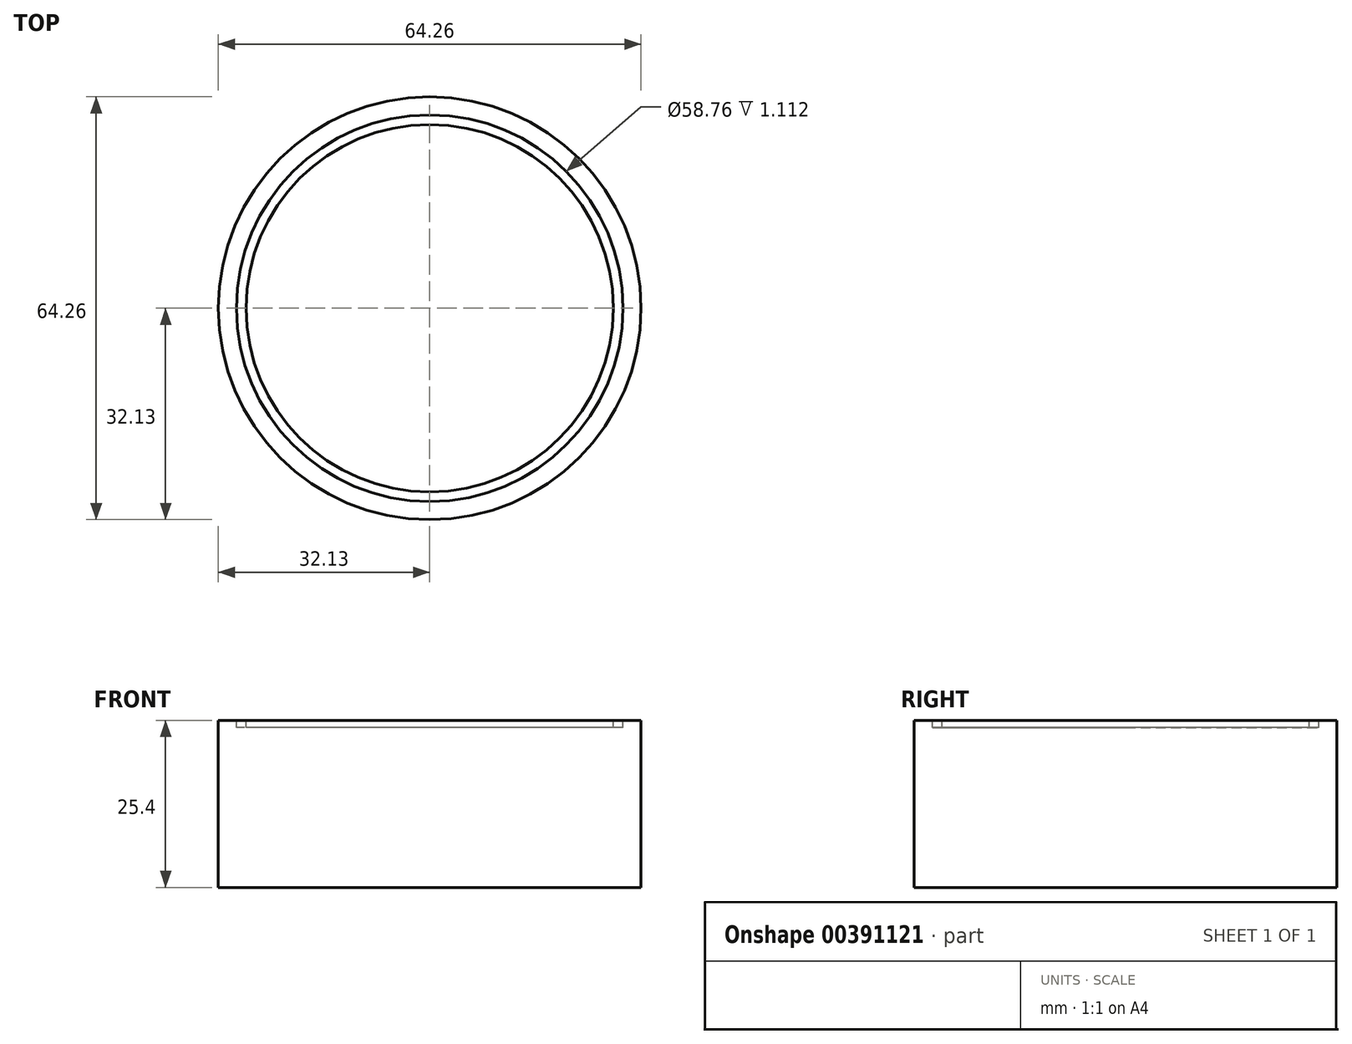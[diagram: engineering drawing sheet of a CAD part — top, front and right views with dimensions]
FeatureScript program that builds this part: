
annotation { "Feature Type Name" : "Feature", "Feature Type Description" : "" }
export const myFeature = defineFeature(function(context is Context, id is Id, definition is map)
    precondition{}
    {
        {
            var Q0;
            Q0=qCreatedBy(makeId("Top.planeOp"),FACE);
            var sketch = newSketch(context, id + "F0", { "sketchPlane" : qUnion([Q0])});
            skCircle(sketch, "E0", {"center": v(0, 0) * mm, "radius": 32.13 * mm});
            skSolve(sketch);
        }
        {
            var Q0;
            Q0 = qSketchRegion(id + "F0", true);
            extrude(context, id + "F1", {"entities" : qUnion([Q0]), "depth" : 25.4 * mm});
        }
        {
            var Q0;
            Q0=makeQuery(id+"F1.opExtrude","CAP_FACE",FACE,{"disambiguationData":[OSD([sQuery(id+"F0.wireOp",EDGE,"E0")])],"isStart":false});
            var sketch = newSketch(context, id + "F2", { "sketchPlane" : qUnion([Q0])});
            skCircle(sketch, "E1", {"center": v(0, 0) * mm, "radius": 29.38 * mm});
            skCircle(sketch, "E2", {"center": v(0, 0) * mm, "radius": 27.92 * mm});
            skSolve(sketch);
        }
        {
            var Q0;
            Q0=makeQuery(id+"F2.imprint","IMPRINT",FACE,{"disambiguationData":[TD([[makeQuery(id+"F2.imprint","IMPRINT",EDGE,{"derivedFrom":sQuery(id+"F2.wireOp",EDGE,"E1")}),1.0]])]});
            var Q1;
            Q1=sQuery(id+"F2.wireOp",EDGE,"E2");
            var Q2;
            Q2=sQuery(id+"F2.wireOp",EDGE,"E1");
            extrude(context, id + "F3", {"entities" : qUnion([Q0]), "operationType" : NewBodyOperationType.REMOVE, "surfaceEntities" : qUnion([Q1, Q2]), "oppositeDirection" : true, "depth" : 1.11 * mm});
        }
    });
